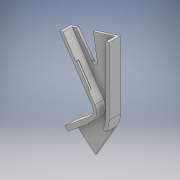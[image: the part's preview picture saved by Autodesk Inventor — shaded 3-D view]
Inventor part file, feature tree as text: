
AUTODESK INVENTOR PART (.ipt)
format: ipt  version: 2017 (Build 210142000, 142)  size: 186,368 bytes
history: native  units: mm
features: extrude x5, sketch x4, chamfer x1
ambient origin geometry x8: Origin, YZ Plane, XZ Plane, XY Plane, X Axis, Y Axis, Z Axis, Center Point
bodies: Solid1 (feature_tree)
feature tree (10):
  sketch  "Sketch1"  dims[d0=38.0mm d1=13.0mm d2=9.0mm d3=5.0mm d4=30.0deg d5=23.0mm d6=6.0mm d7=4.0mm d8=38.0mm d9=30.0deg d10=23.0mm d11=6.0mm d12=4.0mm d13=1.5mm]
  extrude  "Extrusion1"  Depth=1.5mm
  extrude  "Extrusion2"  Depth=1.5mm
  extrude  "Extrusion4"  Depth=12.730996mm
  extrude  "Extrusion5"  Depth=10.0mm
  chamfer  "Chamfer1"  Distance=15.0mm
  extrude  "Extrusion6"  Depth=1.0mm TaperAngle=0.0deg
  sketch  "Sketch2"  dims[d14=1.5mm d15=13.885952mm]
  sketch  "Sketch3"  dims[d16=13.885952mm d17=12.730996mm]
  sketch  "Sketch4"  dims[d18=12.730996mm d19=30.0mm d20=15.0mm d21=1.0mm d22=0.0mm d23=4.0mm d24=0.0mm d28=12.0mm d29=0.5mm d30=0.0mm d31=10.0mm d32=5.0mm d33=1.0mm d34=0.5mm d35=0.0mm d36=0.25mm d37=2.0mm d38=45.0deg d39=10.0mm d40=0.0mm]
